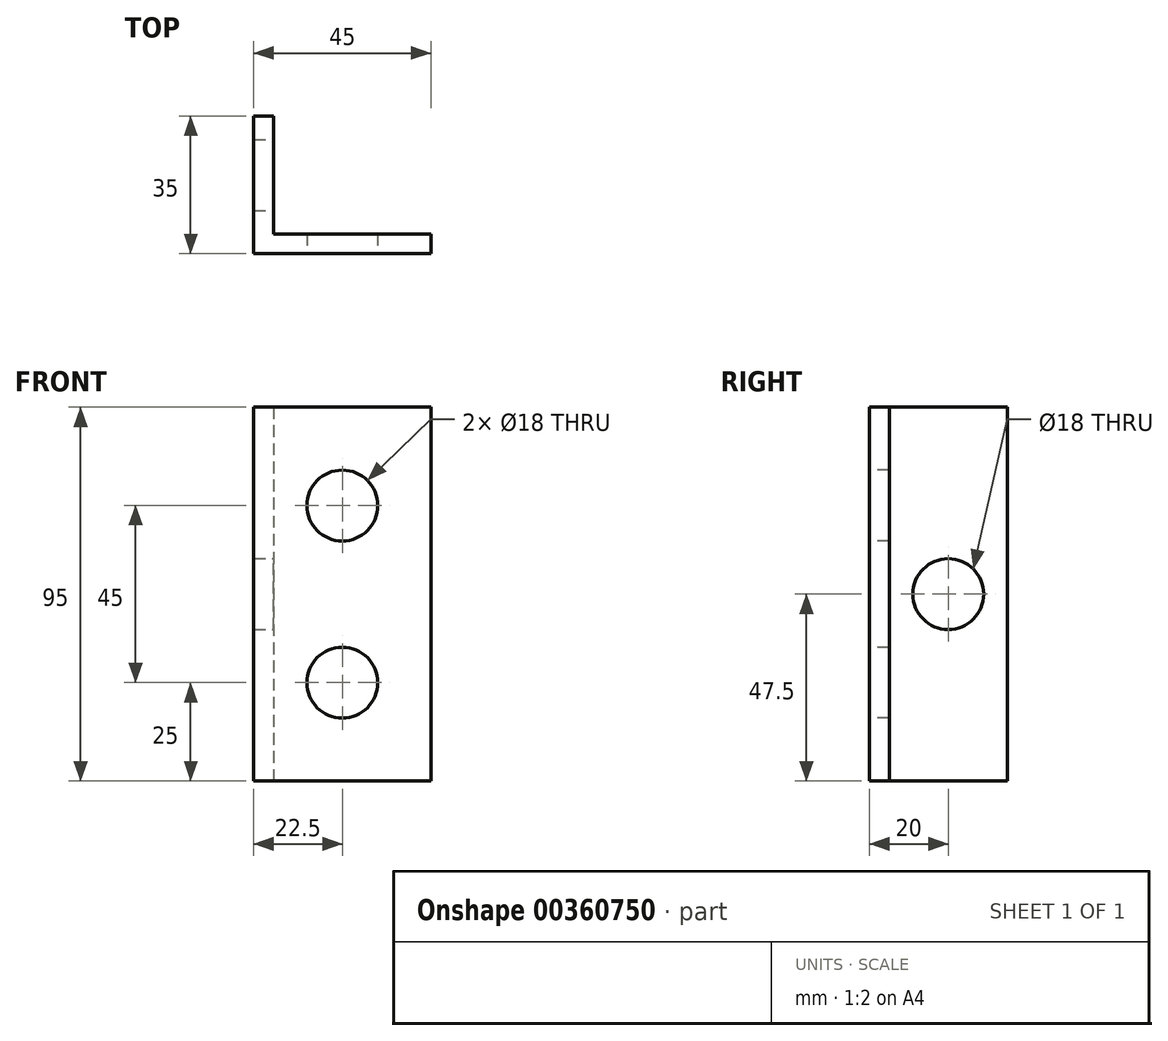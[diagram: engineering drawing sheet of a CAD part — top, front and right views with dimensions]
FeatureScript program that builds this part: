
annotation { "Feature Type Name" : "Feature", "Feature Type Description" : "" }
export const myFeature = defineFeature(function(context is Context, id is Id, definition is map)
    precondition{}
    {
        {
            var Q0;
            Q0=qCreatedBy(makeId("Top.planeOp"),FACE);
            var sketch = newSketch(context, id + "F0", { "sketchPlane" : qUnion([Q0])});
            skLineSegment(sketch, "E0", {"start": v(0, 30) * mm, "end": v(0, 0) * mm});
            skLineSegment(sketch, "E1", {"start": v(0, 0) * mm, "end": v(40, 0) * mm});
            skLineSegment(sketch, "E2", {"start": v(0, 30) * mm, "end": v(-5, 30) * mm});
            skLineSegment(sketch, "E3", {"start": v(-5, 30) * mm, "end": v(-5, -5) * mm});
            skLineSegment(sketch, "E4", {"start": v(-5, -5) * mm, "end": v(40, -5) * mm});
            skLineSegment(sketch, "E5", {"start": v(40, 0) * mm, "end": v(40, -5) * mm});
            skSolve(sketch);
        }
        {
            var Q0;
            Q0=makeQuery(id+"F0.imprint","IMPRINT",FACE,{"disambiguationData":[TD([[makeQuery(id+"F0.imprint","IMPRINT",EDGE,{"derivedFrom":sQuery(id+"F0.wireOp",EDGE,"E0")}),-1.0]])]});
            extrude(context, id + "F1", {"entities" : qUnion([Q0]), "depth" : 95 * mm});
        }
        {
            var Q0;
            Q0=makeQuery(id+"F1.opExtrude","SWEPT_FACE",FACE,{"disambiguationData":[OSD([sQuery(id+"F0.wireOp",EDGE,"E4")])]});
            var sketch = newSketch(context, id + "F2", { "sketchPlane" : qUnion([Q0])});
            skCircle(sketch, "E6", {"center": v(17.5, 70) * mm, "radius": 9 * mm});
            skCircle(sketch, "E7", {"center": v(17.5, 25) * mm, "radius": 9 * mm});
            skSolve(sketch);
        }
        {
            var Q0;
            Q0=qSketchRegion(id+"F2",true);
            extrude(context, id + "F3", {"entities" : qUnion([Q0]), "operationType" : NewBodyOperationType.REMOVE, "oppositeDirection" : true, "depth" : 25 * mm});
        }
        {
            var Q0;
            Q0=makeQuery(id+"F1.opExtrude","SWEPT_FACE",FACE,{"disambiguationData":[OSD([sQuery(id+"F0.wireOp",EDGE,"E0")])]});
            var sketch = newSketch(context, id + "F4", { "sketchPlane" : qUnion([Q0])});
            skCircle(sketch, "E8", {"center": v(15, 47.5) * mm, "radius": 9 * mm});
            skSolve(sketch);
        }
        {
            var Q0;
            Q0=qSketchRegion(id+"F4",true);
            extrude(context, id + "F5", {"entities" : qUnion([Q0]), "operationType" : NewBodyOperationType.REMOVE, "oppositeDirection" : true, "depth" : 25 * mm});
        }
    });
